# Revit family: 1000_Sliding_Window_XOX_Standard
name_source: partatom
category: Windows
revit_build: Autodesk Revit 2014 (Build: 20130308_1515(x64)
units: mm (PartAtom-declared; Revit-internal decimal feet)

## types (120) — shared parameters
Centered In Wall = Yes
Custom Sash Width Middle = 100 mm  [stored 0.328084 ft]
Default Sill Height = 800 mm
Description = Sliding window, XOX
Equal Sash Width = Yes
Frame Thickness = 76 mm
Limit Sash Height Max = 1800 mm  [stored 5.90551 ft]
Limit Sash Height Min = 300 mm
Limit Sash Width Max = 1500 mm  [stored 4.92126 ft]
Limit Sash Width Middle Min = 300 mm
Limit Sash Width Min = 300 mm
Limit Window Height Max = 1857 mm
Limit Window Height Min = 357 mm
Limit Window Width Max = 4440 mm
Limit Window Width Min = 840 mm
Manufacturer = Crealco
Model = 1000
Sash Frame Seal = 2 mm  [stored 0.00656168 ft]
URL = http://www.crealco.co.za
Wall Closure = By host
zero-valued in all types: Custom Frame Offset From Exterior

## per-type parameters (varying)
| type | Area Middle Sash Glazing | Area Side Sash Glazing | Clearvue SHGC Value | Clearvue U Value | Custom Windload | Custom Window Height | Custom Window Width | Energy Advantage SHGC Value | Energy Advantage U Value | Heavy Duty Interlocker | Height | Intruderprufe LowE SHGC Value | Intruderprufe LowE U Value | Intruderprufe SHGC Value | Intruderprufe U Value | Is Heavy Duty Mullion | Limit Sash Width Middle Max | Max Pane Area | Sash Height | Sash Width Middle | Sash Width Sides | Standard Interlocker | Width | Windload Design |
| 1000SW-0906XOX-1000Pa | 0.09 m² | 0.09 m² | 0.535 | 6.31 | 1000 mm  [stored 3.28084 ft] | 590 mm  [stored 1.9357 ft] | 890 mm  [stored 2.91995 ft] | 0.482 | 5.4 | No | 590 mm  [stored 1.9357 ft] | 0.444 | 5.12 | 0.508 | 5.99 | 0 mm  [stored 0 ft] | 350 mm | 0.09 m² | 533 mm | 317 mm | 317 mm | Yes | 890 mm  [stored 2.91995 ft] | 1000 mm  [stored 3.28084 ft] |
| 1000SW-1206XOX-1000Pa | 0.14 m² | 0.14 m² | 0.557 | 6.4 | 1000 mm  [stored 3.28084 ft] | 590 mm  [stored 1.9357 ft] | 1190 mm  [stored 3.9042 ft] | 0.5 | 5.34 | No | 590 mm  [stored 1.9357 ft] | 0.46 | 5.05 | 0.527 | 6.06 | 0 mm  [stored 0 ft] | 650 mm | 0.14 m² | 533 mm | 417 mm | 417 mm | Yes | 1190 mm  [stored 3.9042 ft] | 1000 mm  [stored 3.28084 ft] |
| 1000SW-1506XOX-1000Pa | 0.18 m² | 0.18 m² | 0.569 | 6.45 | 1000 mm  [stored 3.28084 ft] | 590 mm  [stored 1.9357 ft] | 1490 mm  [stored 4.88845 ft] | 0.511 | 5.31 | No | 590 mm  [stored 1.9357 ft] | 0.47 | 5.01 | 0.539 | 6.1 | 0 mm  [stored 0 ft] | 950 mm | 0.18 m² | 533 mm | 517 mm | 517 mm | Yes | 1490 mm  [stored 4.88845 ft] | 1000 mm  [stored 3.28084 ft] |
| 1000SW-1806XOX-1000Pa | 0.22 m² | 0.22 m² | 0.578 | 6.48 | 1000 mm  [stored 3.28084 ft] | 590 mm  [stored 1.9357 ft] | 1790 mm  [stored 5.8727 ft] | 0.519 | 5.29 | No | 590 mm  [stored 1.9357 ft] | 0.476 | 4.98 | 0.547 | 6.13 | 0 mm  [stored 0 ft] | 1250 mm | 0.22 m² | 533 mm | 617 mm | 617 mm | Yes | 1790 mm  [stored 5.8727 ft] | 1000 mm  [stored 3.28084 ft] |
| 1000SW-2106XOX-1000Pa | 0.27 m² | 0.27 m² | 0.584 | 6.51 | 1000 mm  [stored 3.28084 ft] | 590 mm  [stored 1.9357 ft] | 2090 mm  [stored 6.85696 ft] | 0.524 | 5.27 | No | 590 mm  [stored 1.9357 ft] | 0.481 | 4.96 | 0.552 | 6.15 | 0 mm  [stored 0 ft] | 1500 mm  [stored 4.92126 ft] | 0.27 m² | 533 mm | 717 mm | 717 mm | Yes | 2090 mm  [stored 6.85696 ft] | 1000 mm  [stored 3.28084 ft] |
| 1000SW-2406XOX-1000Pa | 0.31 m² | 0.31 m² | 0.588 | 6.52 | 1000 mm  [stored 3.28084 ft] | 590 mm  [stored 1.9357 ft] | 2390 mm  [stored 7.84121 ft] | 0.528 | 5.26 | No | 590 mm  [stored 1.9357 ft] | 0.484 | 4.95 | 0.556 | 6.16 | 0 mm  [stored 0 ft] | 1500 mm  [stored 4.92126 ft] | 0.31 m² | 533 mm | 817 mm | 817 mm | Yes | 2390 mm  [stored 7.84121 ft] | 1000 mm  [stored 3.28084 ft] |
| 1000SW-2706XOX-1000Pa | 0.35 m² | 0.35 m² | 0.592 | 6.54 | 1000 mm  [stored 3.28084 ft] | 590 mm  [stored 1.9357 ft] | 2690 mm | 0.531 | 5.25 | No | 590 mm  [stored 1.9357 ft] | 0.487 | 4.94 | 0.559 | 6.17 | 0 mm  [stored 0 ft] | 1500 mm  [stored 4.92126 ft] | 0.35 m² | 533 mm | 917 mm | 917 mm | Yes | 2690 mm | 1000 mm  [stored 3.28084 ft] |
| 1000SW-3006XOX-1000Pa | 0.4 m² | 0.4 m² | 0.595 | 6.55 | 1000 mm  [stored 3.28084 ft] | 590 mm  [stored 1.9357 ft] | 2990 mm  [stored 9.80971 ft] | 0.533 | 5.24 | No | 590 mm  [stored 1.9357 ft] | 0.489 | 4.93 | 0.562 | 6.18 | 0 mm  [stored 0 ft] | 1500 mm  [stored 4.92126 ft] | 0.4 m² | 533 mm | 1017 mm | 1017 mm | Yes | 2990 mm  [stored 9.80971 ft] | 1000 mm  [stored 3.28084 ft] |
| 1000SW-0909XOX-1000Pa | 0.16 m² | 0.16 m² | 0.603 | 6.11 | 1000 mm  [stored 3.28084 ft] | 890 mm  [stored 2.91995 ft] | 890 mm  [stored 2.91995 ft] | 0.541 | 5.06 | No | 890 mm  [stored 2.91995 ft] | 0.502 | 4.85 | 0.573 | 5.85 | 0 mm  [stored 0 ft] | 350 mm | 0.16 m² | 833 mm | 317 mm | 317 mm | Yes | 890 mm  [stored 2.91995 ft] | 1000 mm  [stored 3.28084 ft] |
| 1000SW-1209XOX-1000Pa | 0.23 m² | 0.23 m² | 0.626 | 6.18 | 1000 mm  [stored 3.28084 ft] | 890 mm  [stored 2.91995 ft] | 1190 mm  [stored 3.9042 ft] | 0.562 | 4.96 | No | 890 mm  [stored 2.91995 ft] | 0.52 | 4.74 | 0.595 | 5.91 | 0 mm  [stored 0 ft] | 650 mm | 0.23 m² | 833 mm | 417 mm | 417 mm | Yes | 1190 mm  [stored 3.9042 ft] | 1000 mm  [stored 3.28084 ft] |
| 1000SW-1509XOX-1000Pa | 0.3 m² | 0.3 m² | 0.641 | 6.22 | 1000 mm  [stored 3.28084 ft] | 890 mm  [stored 2.91995 ft] | 1490 mm  [stored 4.88845 ft] | 0.575 | 4.9 | No | 890 mm  [stored 2.91995 ft] | 0.531 | 4.68 | 0.608 | 5.95 | 0 mm  [stored 0 ft] | 950 mm | 0.3 m² | 833 mm | 517 mm | 517 mm | Yes | 1490 mm  [stored 4.88845 ft] | 1000 mm  [stored 3.28084 ft] |
| 1000SW-1809XOX-1000Pa | 0.38 m² | 0.38 m² | 0.65 | 6.25 | 1000 mm  [stored 3.28084 ft] | 890 mm  [stored 2.91995 ft] | 1790 mm  [stored 5.8727 ft] | 0.583 | 4.87 | No | 890 mm  [stored 2.91995 ft] | 0.538 | 4.64 | 0.616 | 5.97 | 0 mm  [stored 0 ft] | 1250 mm | 0.38 m² | 833 mm | 617 mm | 617 mm | Yes | 1790 mm  [stored 5.8727 ft] | 1000 mm  [stored 3.28084 ft] |
| 1000SW-2109XOX-1000Pa | 0.45 m² | 0.45 m² | 0.657 | 6.27 | 1000 mm  [stored 3.28084 ft] | 890 mm  [stored 2.91995 ft] | 2090 mm  [stored 6.85696 ft] | 0.589 | 4.84 | No | 890 mm  [stored 2.91995 ft] | 0.543 | 4.61 | 0.622 | 5.99 | 0 mm  [stored 0 ft] | 1500 mm  [stored 4.92126 ft] | 0.45 m² | 833 mm | 717 mm | 717 mm | Yes | 2090 mm  [stored 6.85696 ft] | 1000 mm  [stored 3.28084 ft] |
| 1000SW-2409XOX-1000Pa | 0.52 m² | 0.52 m² | 0.662 | 6.28 | 1000 mm  [stored 3.28084 ft] | 890 mm  [stored 2.91995 ft] | 2390 mm  [stored 7.84121 ft] | 0.593 | 4.82 | No | 890 mm  [stored 2.91995 ft] | 0.547 | 4.59 | 0.627 | 6 | 0 mm  [stored 0 ft] | 1500 mm  [stored 4.92126 ft] | 0.52 m² | 833 mm | 817 mm | 817 mm | Yes | 2390 mm  [stored 7.84121 ft] | 1000 mm  [stored 3.28084 ft] |
| 1000SW-2709XOX-1000Pa | 0.6 m² | 0.6 m² | 0.666 | 6.3 | 1000 mm  [stored 3.28084 ft] | 890 mm  [stored 2.91995 ft] | 2690 mm | 0.597 | 4.8 | No | 890 mm  [stored 2.91995 ft] | 0.55 | 4.57 | 0.631 | 6.01 | 0 mm  [stored 0 ft] | 1500 mm  [stored 4.92126 ft] | 0.6 m² | 833 mm | 917 mm | 917 mm | Yes | 2690 mm | 1000 mm  [stored 3.28084 ft] |
| 1000SW-3009XOX-1000Pa | 0.67 m² | 0.67 m² | 0.669 | 6.31 | 1000 mm  [stored 3.28084 ft] | 890 mm  [stored 2.91995 ft] | 2990 mm  [stored 9.80971 ft] | 0.599 | 4.79 | No | 890 mm  [stored 2.91995 ft] | 0.553 | 4.56 | 0.634 | 6.02 | 0 mm  [stored 0 ft] | 1500 mm  [stored 4.92126 ft] | 0.67 m² | 833 mm | 1017 mm | 1017 mm | Yes | 2990 mm  [stored 9.80971 ft] | 1000 mm  [stored 3.28084 ft] |
| 1000SW-0912XOX-1000Pa | 0.22 m² | 0.22 m² | 0.636 | 6.01 | 1000 mm  [stored 3.28084 ft] | 1190 mm  [stored 3.9042 ft] | 890 mm  [stored 2.91995 ft] | 0.571 | 4.89 | No | 1190 mm  [stored 3.9042 ft] | 0.531 | 4.71 | 0.605 | 5.78 | 0 mm  [stored 0 ft] | 350 mm | 0.22 m² | 1133 mm | 317 mm | 317 mm | Yes | 890 mm  [stored 2.91995 ft] | 1000 mm  [stored 3.28084 ft] |
| 1000SW-1212XOX-1000Pa | 0.33 m² | 0.33 m² | 0.661 | 6.07 | 1000 mm  [stored 3.28084 ft] | 1190 mm  [stored 3.9042 ft] | 1190 mm  [stored 3.9042 ft] | 0.593 | 4.77 | No | 1190 mm  [stored 3.9042 ft] | 0.55 | 4.59 | 0.628 | 5.84 | 0 mm  [stored 0 ft] | 650 mm | 0.33 m² | 1133 mm | 417 mm | 417 mm | Yes | 1190 mm  [stored 3.9042 ft] | 1000 mm  [stored 3.28084 ft] |
| 1000SW-1512XOX-1000Pa | 0.43 m² | 0.43 m² | 0.676 | 6.11 | 1000 mm  [stored 3.28084 ft] | 1190 mm  [stored 3.9042 ft] | 1490 mm  [stored 4.88845 ft] | 0.606 | 4.7 | No | 1190 mm  [stored 3.9042 ft] | 0.562 | 4.52 | 0.642 | 5.87 | 0 mm  [stored 0 ft] | 950 mm | 0.43 m² | 1133 mm | 517 mm | 517 mm | Yes | 1490 mm  [stored 4.88845 ft] | 1000 mm  [stored 3.28084 ft] |
| 1000SW-1812XOX-1000Pa | 0.53 m² | 0.53 m² | 0.686 | 6.13 | 1000 mm  [stored 3.28084 ft] | 1190 mm  [stored 3.9042 ft] | 1790 mm  [stored 5.8727 ft] | 0.615 | 4.66 | No | 1190 mm  [stored 3.9042 ft] | 0.569 | 4.47 | 0.651 | 5.89 | 0 mm  [stored 0 ft] | 1250 mm | 0.53 m² | 1133 mm | 617 mm | 617 mm | Yes | 1790 mm  [stored 5.8727 ft] | 1000 mm  [stored 3.28084 ft] |
| 1000SW-2112XOX-1000Pa | 0.64 m² | 0.64 m² | 0.693 | 6.15 | 1000 mm  [stored 3.28084 ft] | 1190 mm  [stored 3.9042 ft] | 2090 mm  [stored 6.85696 ft] | 0.621 | 4.63 | No | 1190 mm  [stored 3.9042 ft] | 0.575 | 4.44 | 0.657 | 5.91 | 0 mm  [stored 0 ft] | 1500 mm  [stored 4.92126 ft] | 0.64 m² | 1133 mm | 717 mm | 717 mm | Yes | 2090 mm  [stored 6.85696 ft] | 1000 mm  [stored 3.28084 ft] |
| 1000SW-2412XOX-1000Pa | 0.74 m² | 0.74 m² | 0.699 | 6.17 | 1000 mm  [stored 3.28084 ft] | 1190 mm  [stored 3.9042 ft] | 2390 mm  [stored 7.84121 ft] | 0.625 | 4.6 | No | 1190 mm  [stored 3.9042 ft] | 0.579 | 4.41 | 0.662 | 5.92 | 0 mm  [stored 0 ft] | 1500 mm  [stored 4.92126 ft] | 0.74 m² | 1133 mm | 817 mm | 817 mm | Yes | 2390 mm  [stored 7.84121 ft] | 1000 mm  [stored 3.28084 ft] |
| 1000SW-2712XOX-1000Pa | 0.84 m² | 0.84 m² | 0.703 | 6.18 | 1000 mm  [stored 3.28084 ft] | 1190 mm  [stored 3.9042 ft] | 2690 mm | 0.629 | 4.58 | No | 1190 mm  [stored 3.9042 ft] | 0.582 | 4.39 | 0.666 | 5.93 | 0 mm  [stored 0 ft] | 1500 mm  [stored 4.92126 ft] | 0.84 m² | 1133 mm | 917 mm | 917 mm | Yes | 2690 mm | 1000 mm  [stored 3.28084 ft] |
| 1000SW-3012XOX-1000Pa | 0.95 m² | 0.95 m² | 0.706 | 6.19 | 1000 mm  [stored 3.28084 ft] | 1190 mm  [stored 3.9042 ft] | 2990 mm  [stored 9.80971 ft] | 0.632 | 4.57 | No | 1190 mm  [stored 3.9042 ft] | 0.584 | 4.38 | 0.669 | 5.94 | 0 mm  [stored 0 ft] | 1500 mm  [stored 4.92126 ft] | 0.95 m² | 1133 mm | 1017 mm | 1017 mm | Yes | 2990 mm  [stored 9.80971 ft] | 1000 mm  [stored 3.28084 ft] |
| 1000SW-0915XOX-1000Pa | 0.29 m² | 0.29 m² | 0.656 | 5.95 | 1000 mm  [stored 3.28084 ft] | 1490 mm  [stored 4.88845 ft] | 890 mm  [stored 2.91995 ft] | 0.589 | 4.79 | No | 1490 mm  [stored 4.88845 ft] | 0.548 | 4.63 | 0.624 | 5.74 | 0 mm  [stored 0 ft] | 350 mm | 0.29 m² | 1433 mm | 317 mm | 317 mm | Yes | 890 mm  [stored 2.91995 ft] | 1000 mm  [stored 3.28084 ft] |
| 1000SW-1215XOX-1000Pa | 0.42 m² | 0.42 m² | 0.682 | 6.01 | 1000 mm  [stored 3.28084 ft] | 1490 mm  [stored 4.88845 ft] | 1190 mm  [stored 3.9042 ft] | 0.611 | 4.66 | No | 1490 mm  [stored 4.88845 ft] | 0.568 | 4.5 | 0.648 | 5.79 | 0 mm  [stored 0 ft] | 650 mm | 0.42 m² | 1433 mm | 417 mm | 417 mm | Yes | 1190 mm  [stored 3.9042 ft] | 1000 mm  [stored 3.28084 ft] |
| 1000SW-1515XOX-1000Pa | 0.55 m² | 0.55 m² | 0.698 | 6.04 | 1000 mm  [stored 3.28084 ft] | 1490 mm  [stored 4.88845 ft] | 1490 mm  [stored 4.88845 ft] | 0.625 | 4.58 | No | 1490 mm  [stored 4.88845 ft] | 0.58 | 4.42 | 0.662 | 5.83 | 0 mm  [stored 0 ft] | 950 mm | 0.55 m² | 1433 mm | 517 mm | 517 mm | Yes | 1490 mm  [stored 4.88845 ft] | 1000 mm  [stored 3.28084 ft] |
| 1000SW-1815XOX-1000Pa | 0.69 m² | 0.69 m² | 0.708 | 6.07 | 1000 mm  [stored 3.28084 ft] | 1490 mm  [stored 4.88845 ft] | 1790 mm  [stored 5.8727 ft] | 0.634 | 4.53 | No | 1490 mm  [stored 4.88845 ft] | 0.588 | 4.37 | 0.672 | 5.85 | 0 mm  [stored 0 ft] | 1250 mm | 0.69 m² | 1433 mm | 617 mm | 617 mm | Yes | 1790 mm  [stored 5.8727 ft] | 1000 mm  [stored 3.28084 ft] |
| 1000SW-2115XOX-1000Pa | 0.82 m² | 0.82 m² | 0.715 | 6.08 | 1000 mm  [stored 3.28084 ft] | 1490 mm  [stored 4.88845 ft] | 2090 mm  [stored 6.85696 ft] | 0.64 | 4.5 | No | 1490 mm  [stored 4.88845 ft] | 0.593 | 4.33 | 0.678 | 5.86 | 0 mm  [stored 0 ft] | 1500 mm  [stored 4.92126 ft] | 0.82 m² | 1433 mm | 717 mm | 717 mm | Yes | 2090 mm  [stored 6.85696 ft] | 1000 mm  [stored 3.28084 ft] |
| 1000SW-2415XOX-1000Pa | 0.95 m² | 0.95 m² | 0.721 | 6.1 | 1000 mm  [stored 3.28084 ft] | 1490 mm  [stored 4.88845 ft] | 2390 mm  [stored 7.84121 ft] | 0.645 | 4.47 | No | 1490 mm  [stored 4.88845 ft] | 0.597 | 4.31 | 0.683 | 5.87 | 0 mm  [stored 0 ft] | 1500 mm  [stored 4.92126 ft] | 0.95 m² | 1433 mm | 817 mm | 817 mm | Yes | 2390 mm  [stored 7.84121 ft] | 1000 mm  [stored 3.28084 ft] |
| 1000SW-2715XOX-1000Pa | 1.09 m² | 1.09 m² | 0.725 | 6.11 | 1000 mm  [stored 3.28084 ft] | 1490 mm  [stored 4.88845 ft] | 2690 mm | 0.648 | 4.45 | No | 1490 mm  [stored 4.88845 ft] | 0.601 | 4.29 | 0.687 | 5.88 | 0 mm  [stored 0 ft] | 1500 mm  [stored 4.92126 ft] | 1.09 m² | 1433 mm | 917 mm | 917 mm | Yes | 2690 mm | 1000 mm  [stored 3.28084 ft] |
| 1000SW-3015XOX-1000Pa | 1.22 m² | 1.22 m² | 0.728 | 6.11 | 1000 mm  [stored 3.28084 ft] | 1490 mm  [stored 4.88845 ft] | 2990 mm  [stored 9.80971 ft] | 0.651 | 4.44 | No | 1490 mm  [stored 4.88845 ft] | 0.603 | 4.207 | 0.69 | 5.89 | 0 mm  [stored 0 ft] | 1500 mm  [stored 4.92126 ft] | 1.22 m² | 1433 mm | 1017 mm | 1017 mm | Yes | 2990 mm  [stored 9.80971 ft] | 1000 mm  [stored 3.28084 ft] |
| 1000SW-0918XOX-1000Pa | 0.35 m² | 0.35 m² | 0.669 | 5.91 | 1000 mm  [stored 3.28084 ft] | 1790 mm  [stored 5.8727 ft] | 890 mm  [stored 2.91995 ft] | 0.6 | 4.72 | No | 1790 mm  [stored 5.8727 ft] | 0.559 | 4.58 | 0.637 | 5.71 | 0 mm  [stored 0 ft] | 350 mm | 0.35 m² | 1733 mm | 317 mm | 317 mm | Yes | 890 mm  [stored 2.91995 ft] | 1000 mm  [stored 3.28084 ft] |
| 1000SW-1218XOX-1000Pa | 0.52 m² | 0.52 m² | 0.696 | 5.96 | 1000 mm  [stored 3.28084 ft] | 1790 mm  [stored 5.8727 ft] | 1190 mm  [stored 3.9042 ft] | 0.623 | 4.59 | No | 1790 mm  [stored 5.8727 ft] | 0.58 | 4.44 | 0.661 | 5.76 | 0 mm  [stored 0 ft] | 650 mm | 0.52 m² | 1733 mm | 417 mm | 417 mm | Yes | 1190 mm  [stored 3.9042 ft] | 1000 mm  [stored 3.28084 ft] |
| 1000SW-1518XOX-1000Pa | 0.68 m² | 0.68 m² | 0.712 | 6 | 1000 mm  [stored 3.28084 ft] | 1790 mm  [stored 5.8727 ft] | 1490 mm  [stored 4.88845 ft] | 0.637 | 4.51 | No | 1790 mm  [stored 5.8727 ft] | 0.592 | 4.36 | 0.676 | 5.8 | 0 mm  [stored 0 ft] | 950 mm | 0.68 m² | 1733 mm | 517 mm | 517 mm | Yes | 1490 mm  [stored 4.88845 ft] | 1000 mm  [stored 3.28084 ft] |
| 1000SW-1818XOX-1000Pa | 0.84 m² | 0.84 m² | 0.722 | 6.02 | 1000 mm  [stored 3.28084 ft] | 1790 mm  [stored 5.8727 ft] | 1790 mm  [stored 5.8727 ft] | 0.646 | 4.45 | Yes | 1790 mm  [stored 5.8727 ft] | 0.6 | 4.3 | 0.685 | 5.82 | 1 mm  [stored 0.00328084 ft] | 1250 mm | 0.84 m² | 1733 mm | 617 mm | 617 mm | No | 1790 mm  [stored 5.8727 ft] | 1000 mm  [stored 3.28084 ft] |
| 1000SW-2118XOX-1000Pa | 1.01 m² | 1.01 m² | 0.73 | 6.04 | 1000 mm  [stored 3.28084 ft] | 1790 mm  [stored 5.8727 ft] | 2090 mm  [stored 6.85696 ft] | 0.653 | 4.41 | Yes | 1790 mm  [stored 5.8727 ft] | 0.606 | 4.27 | 0.692 | 5.83 | 1 mm  [stored 0.00328084 ft] | 1500 mm  [stored 4.92126 ft] | 1.01 m² | 1733 mm | 717 mm | 717 mm | No | 2090 mm  [stored 6.85696 ft] | 1000 mm  [stored 3.28084 ft] |
| 1000SW-2418XOX-1000Pa | 1.17 m² | 1.17 m² | 0.735 | 6.05 | 1000 mm  [stored 3.28084 ft] | 1790 mm  [stored 5.8727 ft] | 2390 mm  [stored 7.84121 ft] | 0.658 | 4.39 | Yes | 1790 mm  [stored 5.8727 ft] | 0.61 | 4.24 | 0.697 | 5.84 | 1 mm  [stored 0.00328084 ft] | 1500 mm  [stored 4.92126 ft] | 1.17 m² | 1733 mm | 817 mm | 817 mm | No | 2390 mm  [stored 7.84121 ft] | 1000 mm  [stored 3.28084 ft] |
| 1000SW-2718XOX-1000Pa | 1.33 m² | 1.33 m² | 0.74 | 6.06 | 1000 mm  [stored 3.28084 ft] | 1790 mm  [stored 5.8727 ft] | 2690 mm | 0.661 | 4.36 | Yes | 1790 mm  [stored 5.8727 ft] | 0.613 | 4.21 | 0.701 | 5.85 | 1 mm  [stored 0.00328084 ft] | 1500 mm  [stored 4.92126 ft] | 1.33 m² | 1733 mm | 917 mm | 917 mm | No | 2690 mm | 1000 mm  [stored 3.28084 ft] |
| 1000SW-3018XOX-1000Pa | 1.49 m² | 1.5 m² | 0.743 | 6.07 | 1000 mm  [stored 3.28084 ft] | 1790 mm  [stored 5.8727 ft] | 2990 mm  [stored 9.80971 ft] | 0.664 | 4.35 | Yes | 1790 mm  [stored 5.8727 ft] | 0.616 | 4.2 | 0.704 | 5.86 | 1 mm  [stored 0.00328084 ft] | 1500 mm  [stored 4.92126 ft] | 1.5 m² | 1733 mm | 1017 mm | 1017 mm | No | 2990 mm  [stored 9.80971 ft] | 1000 mm  [stored 3.28084 ft] |
| 1000SW-0906XOX-1500Pa | 0.09 m² | 0.09 m² | 0.535 | 6.31 | 1500 mm  [stored 4.92126 ft] | 590 mm  [stored 1.9357 ft] | 890 mm  [stored 2.91995 ft] | 0.482 | 5.4 | No | 590 mm  [stored 1.9357 ft] | 0.444 | 5.12 | 0.508 | 5.99 | 0 mm  [stored 0 ft] | 350 mm | 0.09 m² | 533 mm | 317 mm | 317 mm | Yes | 890 mm  [stored 2.91995 ft] | 1500 mm  [stored 4.92126 ft] |
| 1000SW-0906XOX-2000Pa | 0.09 m² | 0.09 m² | 0.535 | 6.31 | 2000 mm  [stored 6.56168 ft] | 590 mm  [stored 1.9357 ft] | 890 mm  [stored 2.91995 ft] | 0.482 | 5.4 | No | 590 mm  [stored 1.9357 ft] | 0.444 | 5.12 | 0.508 | 5.99 | 0 mm  [stored 0 ft] | 350 mm | 0.09 m² | 533 mm | 317 mm | 317 mm | Yes | 890 mm  [stored 2.91995 ft] | 2000 mm  [stored 6.56168 ft] |
| 1000SW-0909XOX-1500Pa | 0.16 m² | 0.16 m² | 0.603 | 6.11 | 1500 mm  [stored 4.92126 ft] | 890 mm  [stored 2.91995 ft] | 890 mm  [stored 2.91995 ft] | 0.541 | 5.06 | No | 890 mm  [stored 2.91995 ft] | 0.502 | 4.85 | 0.573 | 5.85 | 0 mm  [stored 0 ft] | 350 mm | 0.16 m² | 833 mm | 317 mm | 317 mm | Yes | 890 mm  [stored 2.91995 ft] | 1500 mm  [stored 4.92126 ft] |
| 1000SW-0909XOX-2000Pa | 0.16 m² | 0.16 m² | 0.603 | 6.11 | 2000 mm  [stored 6.56168 ft] | 890 mm  [stored 2.91995 ft] | 890 mm  [stored 2.91995 ft] | 0.541 | 5.06 | No | 890 mm  [stored 2.91995 ft] | 0.502 | 4.85 | 0.573 | 5.85 | 0 mm  [stored 0 ft] | 350 mm | 0.16 m² | 833 mm | 317 mm | 317 mm | Yes | 890 mm  [stored 2.91995 ft] | 2000 mm  [stored 6.56168 ft] |
| 1000SW-0912XOX-1500Pa | 0.22 m² | 0.22 m² | 0.636 | 6.01 | 1500 mm  [stored 4.92126 ft] | 1190 mm  [stored 3.9042 ft] | 890 mm  [stored 2.91995 ft] | 0.571 | 4.89 | No | 1190 mm  [stored 3.9042 ft] | 0.531 | 4.71 | 0.605 | 5.78 | 0 mm  [stored 0 ft] | 350 mm | 0.22 m² | 1133 mm | 317 mm | 317 mm | Yes | 890 mm  [stored 2.91995 ft] | 1500 mm  [stored 4.92126 ft] |
| 1000SW-0912XOX-2000Pa | 0.22 m² | 0.22 m² | 0.636 | 6.01 | 2000 mm  [stored 6.56168 ft] | 1190 mm  [stored 3.9042 ft] | 890 mm  [stored 2.91995 ft] | 0.571 | 4.89 | No | 1190 mm  [stored 3.9042 ft] | 0.531 | 4.71 | 0.605 | 5.78 | 0 mm  [stored 0 ft] | 350 mm | 0.22 m² | 1133 mm | 317 mm | 317 mm | Yes | 890 mm  [stored 2.91995 ft] | 2000 mm  [stored 6.56168 ft] |
| 1000SW-0915XOX-1500Pa | 0.29 m² | 0.29 m² | 0.656 | 5.95 | 1500 mm  [stored 4.92126 ft] | 1490 mm  [stored 4.88845 ft] | 890 mm  [stored 2.91995 ft] | 0.589 | 4.79 | No | 1490 mm  [stored 4.88845 ft] | 0.548 | 4.63 | 0.624 | 5.74 | 0 mm  [stored 0 ft] | 350 mm | 0.29 m² | 1433 mm | 317 mm | 317 mm | Yes | 890 mm  [stored 2.91995 ft] | 1500 mm  [stored 4.92126 ft] |
| 1000SW-0915XOX-2000Pa | 0.29 m² | 0.29 m² | 0.656 | 5.95 | 2000 mm  [stored 6.56168 ft] | 1490 mm  [stored 4.88845 ft] | 890 mm  [stored 2.91995 ft] | 0.589 | 4.79 | No | 1490 mm  [stored 4.88845 ft] | 0.548 | 4.63 | 0.624 | 5.74 | 0 mm  [stored 0 ft] | 350 mm | 0.29 m² | 1433 mm | 317 mm | 317 mm | Yes | 890 mm  [stored 2.91995 ft] | 2000 mm  [stored 6.56168 ft] |
| 1000SW-0918XOX-1500Pa | 0.35 m² | 0.35 m² | 0.669 | 5.91 | 1500 mm  [stored 4.92126 ft] | 1790 mm  [stored 5.8727 ft] | 890 mm  [stored 2.91995 ft] | 0.6 | 4.72 | No | 1790 mm  [stored 5.8727 ft] | 0.559 | 4.58 | 0.637 | 5.71 | 0 mm  [stored 0 ft] | 350 mm | 0.35 m² | 1733 mm | 317 mm | 317 mm | Yes | 890 mm  [stored 2.91995 ft] | 1500 mm  [stored 4.92126 ft] |
| 1000SW-0918XOX-2000Pa | 0.35 m² | 0.35 m² | 0.669 | 5.91 | 2000 mm  [stored 6.56168 ft] | 1790 mm  [stored 5.8727 ft] | 890 mm  [stored 2.91995 ft] | 0.6 | 4.72 | Yes | 1790 mm  [stored 5.8727 ft] | 0.559 | 4.58 | 0.637 | 5.71 | 1 mm  [stored 0.00328084 ft] | 350 mm | 0.35 m² | 1733 mm | 317 mm | 317 mm | No | 890 mm  [stored 2.91995 ft] | 2000 mm  [stored 6.56168 ft] |
| 1000SW-1206XOX-1500Pa | 0.14 m² | 0.14 m² | 0.557 | 6.4 | 1500 mm  [stored 4.92126 ft] | 590 mm  [stored 1.9357 ft] | 1190 mm  [stored 3.9042 ft] | 0.5 | 5.34 | No | 590 mm  [stored 1.9357 ft] | 0.46 | 5.05 | 0.527 | 6.06 | 0 mm  [stored 0 ft] | 650 mm | 0.14 m² | 533 mm | 417 mm | 417 mm | Yes | 1190 mm  [stored 3.9042 ft] | 1500 mm  [stored 4.92126 ft] |
| 1000SW-1206XOX-2000Pa | 0.14 m² | 0.14 m² | 0.557 | 6.4 | 2000 mm  [stored 6.56168 ft] | 590 mm  [stored 1.9357 ft] | 1190 mm  [stored 3.9042 ft] | 0.5 | 5.34 | No | 590 mm  [stored 1.9357 ft] | 0.46 | 5.05 | 0.527 | 6.06 | 0 mm  [stored 0 ft] | 650 mm | 0.14 m² | 533 mm | 417 mm | 417 mm | Yes | 1190 mm  [stored 3.9042 ft] | 2000 mm  [stored 6.56168 ft] |
| 1000SW-1209XOX-1500Pa | 0.23 m² | 0.23 m² | 0.626 | 6.18 | 1500 mm  [stored 4.92126 ft] | 890 mm  [stored 2.91995 ft] | 1190 mm  [stored 3.9042 ft] | 0.562 | 4.96 | No | 890 mm  [stored 2.91995 ft] | 0.52 | 4.74 | 0.595 | 5.91 | 0 mm  [stored 0 ft] | 650 mm | 0.23 m² | 833 mm | 417 mm | 417 mm | Yes | 1190 mm  [stored 3.9042 ft] | 1500 mm  [stored 4.92126 ft] |
| 1000SW-1209XOX-2000Pa | 0.23 m² | 0.23 m² | 0.626 | 6.18 | 2000 mm  [stored 6.56168 ft] | 890 mm  [stored 2.91995 ft] | 1190 mm  [stored 3.9042 ft] | 0.562 | 4.96 | No | 890 mm  [stored 2.91995 ft] | 0.52 | 4.74 | 0.595 | 5.91 | 0 mm  [stored 0 ft] | 650 mm | 0.23 m² | 833 mm | 417 mm | 417 mm | Yes | 1190 mm  [stored 3.9042 ft] | 2000 mm  [stored 6.56168 ft] |
| 1000SW-1212XOX-1500Pa | 0.33 m² | 0.33 m² | 0.661 | 6.07 | 1500 mm  [stored 4.92126 ft] | 1190 mm  [stored 3.9042 ft] | 1190 mm  [stored 3.9042 ft] | 0.593 | 4.77 | No | 1190 mm  [stored 3.9042 ft] | 0.55 | 4.59 | 0.628 | 5.84 | 0 mm  [stored 0 ft] | 650 mm | 0.33 m² | 1133 mm | 417 mm | 417 mm | Yes | 1190 mm  [stored 3.9042 ft] | 1500 mm  [stored 4.92126 ft] |
| 1000SW-1212XOX-2000Pa | 0.33 m² | 0.33 m² | 0.661 | 6.07 | 2000 mm  [stored 6.56168 ft] | 1190 mm  [stored 3.9042 ft] | 1190 mm  [stored 3.9042 ft] | 0.593 | 4.77 | No | 1190 mm  [stored 3.9042 ft] | 0.55 | 4.59 | 0.628 | 5.84 | 0 mm  [stored 0 ft] | 650 mm | 0.33 m² | 1133 mm | 417 mm | 417 mm | Yes | 1190 mm  [stored 3.9042 ft] | 2000 mm  [stored 6.56168 ft] |
| 1000SW-1215XOX-1500Pa | 0.42 m² | 0.42 m² | 0.682 | 6.01 | 1500 mm  [stored 4.92126 ft] | 1490 mm  [stored 4.88845 ft] | 1190 mm  [stored 3.9042 ft] | 0.611 | 4.66 | No | 1490 mm  [stored 4.88845 ft] | 0.568 | 4.5 | 0.648 | 5.79 | 0 mm  [stored 0 ft] | 650 mm | 0.42 m² | 1433 mm | 417 mm | 417 mm | Yes | 1190 mm  [stored 3.9042 ft] | 1500 mm  [stored 4.92126 ft] |
| 1000SW-1215XOX-2000Pa | 0.42 m² | 0.42 m² | 0.682 | 6.01 | 2000 mm  [stored 6.56168 ft] | 1490 mm  [stored 4.88845 ft] | 1190 mm  [stored 3.9042 ft] | 0.611 | 4.66 | No | 1490 mm  [stored 4.88845 ft] | 0.568 | 4.5 | 0.648 | 5.79 | 0 mm  [stored 0 ft] | 650 mm | 0.42 m² | 1433 mm | 417 mm | 417 mm | Yes | 1190 mm  [stored 3.9042 ft] | 2000 mm  [stored 6.56168 ft] |
| 1000SW-1218XOX-1500Pa | 0.52 m² | 0.52 m² | 0.696 | 5.96 | 1500 mm  [stored 4.92126 ft] | 1790 mm  [stored 5.8727 ft] | 1190 mm  [stored 3.9042 ft] | 0.623 | 4.59 | Yes | 1790 mm  [stored 5.8727 ft] | 0.58 | 4.44 | 0.661 | 5.76 | 1 mm  [stored 0.00328084 ft] | 650 mm | 0.52 m² | 1733 mm | 417 mm | 417 mm | No | 1190 mm  [stored 3.9042 ft] | 1500 mm  [stored 4.92126 ft] |
| 1000SW-1218XOX-2000Pa | 0.52 m² | 0.52 m² | 0.696 | 5.96 | 2000 mm  [stored 6.56168 ft] | 1790 mm  [stored 5.8727 ft] | 1190 mm  [stored 3.9042 ft] | 0.623 | 4.59 | Yes | 1790 mm  [stored 5.8727 ft] | 0.58 | 4.44 | 0.661 | 5.76 | 1 mm  [stored 0.00328084 ft] | 650 mm | 0.52 m² | 1733 mm | 417 mm | 417 mm | No | 1190 mm  [stored 3.9042 ft] | 2000 mm  [stored 6.56168 ft] |
| 1000SW-1506XOX-1500Pa | 0.18 m² | 0.18 m² | 0.569 | 6.45 | 1500 mm  [stored 4.92126 ft] | 590 mm  [stored 1.9357 ft] | 1490 mm  [stored 4.88845 ft] | 0.511 | 5.31 | No | 590 mm  [stored 1.9357 ft] | 0.47 | 5.01 | 0.539 | 6.1 | 0 mm  [stored 0 ft] | 950 mm | 0.18 m² | 533 mm | 517 mm | 517 mm | Yes | 1490 mm  [stored 4.88845 ft] | 1500 mm  [stored 4.92126 ft] |
| 1000SW-1506XOX-2000Pa | 0.18 m² | 0.18 m² | 0.569 | 6.45 | 2000 mm  [stored 6.56168 ft] | 590 mm  [stored 1.9357 ft] | 1490 mm  [stored 4.88845 ft] | 0.511 | 5.31 | No | 590 mm  [stored 1.9357 ft] | 0.47 | 5.01 | 0.539 | 6.1 | 0 mm  [stored 0 ft] | 950 mm | 0.18 m² | 533 mm | 517 mm | 517 mm | Yes | 1490 mm  [stored 4.88845 ft] | 2000 mm  [stored 6.56168 ft] |
| 1000SW-1509XOX-1500Pa | 0.3 m² | 0.3 m² | 0.641 | 6.22 | 1500 mm  [stored 4.92126 ft] | 890 mm  [stored 2.91995 ft] | 1490 mm  [stored 4.88845 ft] | 0.575 | 4.9 | No | 890 mm  [stored 2.91995 ft] | 0.531 | 4.68 | 0.608 | 5.95 | 0 mm  [stored 0 ft] | 950 mm | 0.3 m² | 833 mm | 517 mm | 517 mm | Yes | 1490 mm  [stored 4.88845 ft] | 1500 mm  [stored 4.92126 ft] |
| 1000SW-1509XOX-2000Pa | 0.3 m² | 0.3 m² | 0.641 | 6.22 | 2000 mm  [stored 6.56168 ft] | 890 mm  [stored 2.91995 ft] | 1490 mm  [stored 4.88845 ft] | 0.575 | 4.9 | No | 890 mm  [stored 2.91995 ft] | 0.531 | 4.68 | 0.608 | 5.95 | 0 mm  [stored 0 ft] | 950 mm | 0.3 m² | 833 mm | 517 mm | 517 mm | Yes | 1490 mm  [stored 4.88845 ft] | 2000 mm  [stored 6.56168 ft] |
| 1000SW-1512XOX-1500Pa | 0.43 m² | 0.43 m² | 0.676 | 6.11 | 1500 mm  [stored 4.92126 ft] | 1190 mm  [stored 3.9042 ft] | 1490 mm  [stored 4.88845 ft] | 0.606 | 4.7 | No | 1190 mm  [stored 3.9042 ft] | 0.562 | 4.52 | 0.642 | 5.87 | 0 mm  [stored 0 ft] | 950 mm | 0.43 m² | 1133 mm | 517 mm | 517 mm | Yes | 1490 mm  [stored 4.88845 ft] | 1500 mm  [stored 4.92126 ft] |
| 1000SW-1512XOX-2000Pa | 0.43 m² | 0.43 m² | 0.676 | 6.11 | 2000 mm  [stored 6.56168 ft] | 1190 mm  [stored 3.9042 ft] | 1490 mm  [stored 4.88845 ft] | 0.606 | 4.7 | No | 1190 mm  [stored 3.9042 ft] | 0.562 | 4.52 | 0.642 | 5.87 | 0 mm  [stored 0 ft] | 950 mm | 0.43 m² | 1133 mm | 517 mm | 517 mm | Yes | 1490 mm  [stored 4.88845 ft] | 2000 mm  [stored 6.56168 ft] |
| 1000SW-1515XOX-1500Pa | 0.55 m² | 0.55 m² | 0.698 | 6.04 | 1500 mm  [stored 4.92126 ft] | 1490 mm  [stored 4.88845 ft] | 1490 mm  [stored 4.88845 ft] | 0.625 | 4.58 | No | 1490 mm  [stored 4.88845 ft] | 0.58 | 4.42 | 0.662 | 5.83 | 0 mm  [stored 0 ft] | 950 mm | 0.55 m² | 1433 mm | 517 mm | 517 mm | Yes | 1490 mm  [stored 4.88845 ft] | 1500 mm  [stored 4.92126 ft] |
| 1000SW-1515XOX-2000Pa | 0.55 m² | 0.55 m² | 0.698 | 6.04 | 2000 mm  [stored 6.56168 ft] | 1490 mm  [stored 4.88845 ft] | 1490 mm  [stored 4.88845 ft] | 0.625 | 4.58 | Yes | 1490 mm  [stored 4.88845 ft] | 0.58 | 4.42 | 0.662 | 5.83 | 1 mm  [stored 0.00328084 ft] | 950 mm | 0.55 m² | 1433 mm | 517 mm | 517 mm | No | 1490 mm  [stored 4.88845 ft] | 2000 mm  [stored 6.56168 ft] |
| 1000SW-1518XOX-1500Pa | 0.68 m² | 0.68 m² | 0.712 | 6 | 1500 mm  [stored 4.92126 ft] | 1790 mm  [stored 5.8727 ft] | 1490 mm  [stored 4.88845 ft] | 0.637 | 4.51 | Yes | 1790 mm  [stored 5.8727 ft] | 0.592 | 4.36 | 0.676 | 5.8 | 1 mm  [stored 0.00328084 ft] | 950 mm | 0.68 m² | 1733 mm | 517 mm | 517 mm | No | 1490 mm  [stored 4.88845 ft] | 1500 mm  [stored 4.92126 ft] |
| 1000SW-1518XOX-2000Pa | 0.68 m² | 0.68 m² | 0.712 | 6 | 2000 mm  [stored 6.56168 ft] | 1790 mm  [stored 5.8727 ft] | 1490 mm  [stored 4.88845 ft] | 0.637 | 4.51 | Yes | 1790 mm  [stored 5.8727 ft] | 0.592 | 4.36 | 0.676 | 5.8 | 1 mm  [stored 0.00328084 ft] | 950 mm | 0.68 m² | 1733 mm | 517 mm | 517 mm | No | 1490 mm  [stored 4.88845 ft] | 2000 mm  [stored 6.56168 ft] |
| 1000SW-1806XOX-1500Pa | 0.22 m² | 0.22 m² | 0.578 | 6.48 | 1500 mm  [stored 4.92126 ft] | 590 mm  [stored 1.9357 ft] | 1790 mm  [stored 5.8727 ft] | 0.519 | 5.29 | No | 590 mm  [stored 1.9357 ft] | 0.476 | 4.98 | 0.547 | 6.13 | 0 mm  [stored 0 ft] | 1250 mm | 0.22 m² | 533 mm | 617 mm | 617 mm | Yes | 1790 mm  [stored 5.8727 ft] | 1500 mm  [stored 4.92126 ft] |
| 1000SW-1806XOX-2000Pa | 0.22 m² | 0.22 m² | 0.578 | 6.48 | 2000 mm  [stored 6.56168 ft] | 590 mm  [stored 1.9357 ft] | 1790 mm  [stored 5.8727 ft] | 0.519 | 5.29 | No | 590 mm  [stored 1.9357 ft] | 0.476 | 4.98 | 0.547 | 6.13 | 0 mm  [stored 0 ft] | 1250 mm | 0.22 m² | 533 mm | 617 mm | 617 mm | Yes | 1790 mm  [stored 5.8727 ft] | 2000 mm  [stored 6.56168 ft] |
| 1000SW-1809XOX-1500Pa | 0.38 m² | 0.38 m² | 0.65 | 6.25 | 1500 mm  [stored 4.92126 ft] | 890 mm  [stored 2.91995 ft] | 1790 mm  [stored 5.8727 ft] | 0.583 | 4.87 | No | 890 mm  [stored 2.91995 ft] | 0.538 | 4.64 | 0.616 | 5.97 | 0 mm  [stored 0 ft] | 1250 mm | 0.38 m² | 833 mm | 617 mm | 617 mm | Yes | 1790 mm  [stored 5.8727 ft] | 1500 mm  [stored 4.92126 ft] |
| 1000SW-1809XOX-2000Pa | 0.38 m² | 0.38 m² | 0.65 | 6.25 | 2000 mm  [stored 6.56168 ft] | 890 mm  [stored 2.91995 ft] | 1790 mm  [stored 5.8727 ft] | 0.583 | 4.87 | No | 890 mm  [stored 2.91995 ft] | 0.538 | 4.64 | 0.616 | 5.97 | 0 mm  [stored 0 ft] | 1250 mm | 0.38 m² | 833 mm | 617 mm | 617 mm | Yes | 1790 mm  [stored 5.8727 ft] | 2000 mm  [stored 6.56168 ft] |
| 1000SW-1812XOX-1500Pa | 0.53 m² | 0.53 m² | 0.686 | 6.13 | 1500 mm  [stored 4.92126 ft] | 1190 mm  [stored 3.9042 ft] | 1790 mm  [stored 5.8727 ft] | 0.615 | 4.66 | No | 1190 mm  [stored 3.9042 ft] | 0.569 | 4.47 | 0.651 | 5.89 | 0 mm  [stored 0 ft] | 1250 mm | 0.53 m² | 1133 mm | 617 mm | 617 mm | Yes | 1790 mm  [stored 5.8727 ft] | 1500 mm  [stored 4.92126 ft] |
| 1000SW-1812XOX-2000Pa | 0.53 m² | 0.53 m² | 0.686 | 6.13 | 2000 mm  [stored 6.56168 ft] | 1190 mm  [stored 3.9042 ft] | 1790 mm  [stored 5.8727 ft] | 0.615 | 4.66 | No | 1190 mm  [stored 3.9042 ft] | 0.569 | 4.47 | 0.651 | 5.89 | 0 mm  [stored 0 ft] | 1250 mm | 0.53 m² | 1133 mm | 617 mm | 617 mm | Yes | 1790 mm  [stored 5.8727 ft] | 2000 mm  [stored 6.56168 ft] |
| 1000SW-1815XOX-1500Pa | 0.69 m² | 0.69 m² | 0.708 | 6.07 | 1500 mm  [stored 4.92126 ft] | 1490 mm  [stored 4.88845 ft] | 1790 mm  [stored 5.8727 ft] | 0.634 | 4.53 | No | 1490 mm  [stored 4.88845 ft] | 0.588 | 4.37 | 0.672 | 5.85 | 0 mm  [stored 0 ft] | 1250 mm | 0.69 m² | 1433 mm | 617 mm | 617 mm | Yes | 1790 mm  [stored 5.8727 ft] | 1500 mm  [stored 4.92126 ft] |
| 1000SW-1815XOX-2000Pa | 0.69 m² | 0.69 m² | 0.708 | 6.07 | 2000 mm  [stored 6.56168 ft] | 1490 mm  [stored 4.88845 ft] | 1790 mm  [stored 5.8727 ft] | 0.634 | 4.53 | Yes | 1490 mm  [stored 4.88845 ft] | 0.588 | 4.37 | 0.672 | 5.85 | 1 mm  [stored 0.00328084 ft] | 1250 mm | 0.69 m² | 1433 mm | 617 mm | 617 mm | No | 1790 mm  [stored 5.8727 ft] | 2000 mm  [stored 6.56168 ft] |
| 1000SW-1818XOX-1500Pa | 0.84 m² | 0.84 m² | 0.722 | 6.02 | 1500 mm  [stored 4.92126 ft] | 1790 mm  [stored 5.8727 ft] | 1790 mm  [stored 5.8727 ft] | 0.646 | 4.45 | Yes | 1790 mm  [stored 5.8727 ft] | 0.6 | 4.3 | 0.685 | 5.82 | 1 mm  [stored 0.00328084 ft] | 1250 mm | 0.84 m² | 1733 mm | 617 mm | 617 mm | No | 1790 mm  [stored 5.8727 ft] | 1500 mm  [stored 4.92126 ft] |
| 1000SW-1818XOX-2000Pa | 0.84 m² | 0.84 m² | 0.722 | 6.02 | 2000 mm  [stored 6.56168 ft] | 1790 mm  [stored 5.8727 ft] | 1790 mm  [stored 5.8727 ft] | 0.646 | 4.45 | Yes | 1790 mm  [stored 5.8727 ft] | 0.6 | 4.3 | 0.685 | 5.82 | 1 mm  [stored 0.00328084 ft] | 1250 mm | 0.84 m² | 1733 mm | 617 mm | 617 mm | No | 1790 mm  [stored 5.8727 ft] | 2000 mm  [stored 6.56168 ft] |
| 1000SW-2106XOX-1500Pa | 0.27 m² | 0.27 m² | 0.584 | 6.51 | 1500 mm  [stored 4.92126 ft] | 590 mm  [stored 1.9357 ft] | 2090 mm  [stored 6.85696 ft] | 0.524 | 5.27 | No | 590 mm  [stored 1.9357 ft] | 0.481 | 4.96 | 0.552 | 6.15 | 0 mm  [stored 0 ft] | 1500 mm  [stored 4.92126 ft] | 0.27 m² | 533 mm | 717 mm | 717 mm | Yes | 2090 mm  [stored 6.85696 ft] | 1500 mm  [stored 4.92126 ft] |
| 1000SW-2106XOX-2000Pa | 0.27 m² | 0.27 m² | 0.584 | 6.51 | 2000 mm  [stored 6.56168 ft] | 590 mm  [stored 1.9357 ft] | 2090 mm  [stored 6.85696 ft] | 0.524 | 5.27 | No | 590 mm  [stored 1.9357 ft] | 0.481 | 4.96 | 0.552 | 6.15 | 0 mm  [stored 0 ft] | 1500 mm  [stored 4.92126 ft] | 0.27 m² | 533 mm | 717 mm | 717 mm | Yes | 2090 mm  [stored 6.85696 ft] | 2000 mm  [stored 6.56168 ft] |
| 1000SW-2109XOX-1500Pa | 0.45 m² | 0.45 m² | 0.657 | 6.27 | 1500 mm  [stored 4.92126 ft] | 890 mm  [stored 2.91995 ft] | 2090 mm  [stored 6.85696 ft] | 0.589 | 4.84 | No | 890 mm  [stored 2.91995 ft] | 0.543 | 4.61 | 0.622 | 5.99 | 0 mm  [stored 0 ft] | 1500 mm  [stored 4.92126 ft] | 0.45 m² | 833 mm | 717 mm | 717 mm | Yes | 2090 mm  [stored 6.85696 ft] | 1500 mm  [stored 4.92126 ft] |
| 1000SW-2109XOX-2000Pa | 0.45 m² | 0.45 m² | 0.657 | 6.27 | 2000 mm  [stored 6.56168 ft] | 890 mm  [stored 2.91995 ft] | 2090 mm  [stored 6.85696 ft] | 0.589 | 4.84 | No | 890 mm  [stored 2.91995 ft] | 0.543 | 4.61 | 0.622 | 5.99 | 0 mm  [stored 0 ft] | 1500 mm  [stored 4.92126 ft] | 0.45 m² | 833 mm | 717 mm | 717 mm | Yes | 2090 mm  [stored 6.85696 ft] | 2000 mm  [stored 6.56168 ft] |
| 1000SW-2112XOX-1500Pa | 0.64 m² | 0.64 m² | 0.693 | 6.15 | 1500 mm  [stored 4.92126 ft] | 1190 mm  [stored 3.9042 ft] | 2090 mm  [stored 6.85696 ft] | 0.621 | 4.63 | No | 1190 mm  [stored 3.9042 ft] | 0.575 | 4.44 | 0.657 | 5.91 | 0 mm  [stored 0 ft] | 1500 mm  [stored 4.92126 ft] | 0.64 m² | 1133 mm | 717 mm | 717 mm | Yes | 2090 mm  [stored 6.85696 ft] | 1500 mm  [stored 4.92126 ft] |
| 1000SW-2112XOX-2000Pa | 0.64 m² | 0.64 m² | 0.693 | 6.15 | 2000 mm  [stored 6.56168 ft] | 1190 mm  [stored 3.9042 ft] | 2090 mm  [stored 6.85696 ft] | 0.621 | 4.63 | No | 1190 mm  [stored 3.9042 ft] | 0.575 | 4.44 | 0.657 | 5.91 | 0 mm  [stored 0 ft] | 1500 mm  [stored 4.92126 ft] | 0.64 m² | 1133 mm | 717 mm | 717 mm | Yes | 2090 mm  [stored 6.85696 ft] | 2000 mm  [stored 6.56168 ft] |
| 1000SW-2115XOX-1500Pa | 0.82 m² | 0.82 m² | 0.715 | 6.08 | 1500 mm  [stored 4.92126 ft] | 1490 mm  [stored 4.88845 ft] | 2090 mm  [stored 6.85696 ft] | 0.64 | 4.5 | Yes | 1490 mm  [stored 4.88845 ft] | 0.593 | 4.33 | 0.678 | 5.86 | 1 mm  [stored 0.00328084 ft] | 1500 mm  [stored 4.92126 ft] | 0.82 m² | 1433 mm | 717 mm | 717 mm | No | 2090 mm  [stored 6.85696 ft] | 1500 mm  [stored 4.92126 ft] |
| 1000SW-2115XOX-2000Pa | 0.82 m² | 0.82 m² | 0.715 | 6.08 | 2000 mm  [stored 6.56168 ft] | 1490 mm  [stored 4.88845 ft] | 2090 mm  [stored 6.85696 ft] | 0.64 | 4.5 | Yes | 1490 mm  [stored 4.88845 ft] | 0.593 | 4.33 | 0.678 | 5.86 | 1 mm  [stored 0.00328084 ft] | 1500 mm  [stored 4.92126 ft] | 0.82 m² | 1433 mm | 717 mm | 717 mm | No | 2090 mm  [stored 6.85696 ft] | 2000 mm  [stored 6.56168 ft] |
| 1000SW-2118XOX-1500Pa | 1.01 m² | 1.01 m² | 0.73 | 6.04 | 1500 mm  [stored 4.92126 ft] | 1790 mm  [stored 5.8727 ft] | 2090 mm  [stored 6.85696 ft] | 0.653 | 4.41 | Yes | 1790 mm  [stored 5.8727 ft] | 0.606 | 4.27 | 0.692 | 5.83 | 1 mm  [stored 0.00328084 ft] | 1500 mm  [stored 4.92126 ft] | 1.01 m² | 1733 mm | 717 mm | 717 mm | No | 2090 mm  [stored 6.85696 ft] | 1500 mm  [stored 4.92126 ft] |
| 1000SW-2118XOX-2000Pa | 1.01 m² | 1.01 m² | 0.73 | 6.04 | 2000 mm  [stored 6.56168 ft] | 1790 mm  [stored 5.8727 ft] | 2090 mm  [stored 6.85696 ft] | 0.653 | 4.41 | Yes | 1790 mm  [stored 5.8727 ft] | 0.606 | 4.27 | 0.692 | 5.83 | 1 mm  [stored 0.00328084 ft] | 1500 mm  [stored 4.92126 ft] | 1.01 m² | 1733 mm | 717 mm | 717 mm | No | 2090 mm  [stored 6.85696 ft] | 2000 mm  [stored 6.56168 ft] |
| 1000SW-2406XOX-1500Pa | 0.31 m² | 0.31 m² | 0.588 | 6.52 | 1500 mm  [stored 4.92126 ft] | 590 mm  [stored 1.9357 ft] | 2390 mm  [stored 7.84121 ft] | 0.528 | 5.26 | No | 590 mm  [stored 1.9357 ft] | 0.484 | 4.95 | 0.556 | 6.16 | 0 mm  [stored 0 ft] | 1500 mm  [stored 4.92126 ft] | 0.31 m² | 533 mm | 817 mm | 817 mm | Yes | 2390 mm  [stored 7.84121 ft] | 1500 mm  [stored 4.92126 ft] |
| 1000SW-2406XOX-2000Pa | 0.31 m² | 0.31 m² | 0.588 | 6.52 | 2000 mm  [stored 6.56168 ft] | 590 mm  [stored 1.9357 ft] | 2390 mm  [stored 7.84121 ft] | 0.528 | 5.26 | No | 590 mm  [stored 1.9357 ft] | 0.484 | 4.95 | 0.556 | 6.16 | 0 mm  [stored 0 ft] | 1500 mm  [stored 4.92126 ft] | 0.31 m² | 533 mm | 817 mm | 817 mm | Yes | 2390 mm  [stored 7.84121 ft] | 2000 mm  [stored 6.56168 ft] |
| 1000SW-2409XOX-1500Pa | 0.52 m² | 0.52 m² | 0.662 | 6.28 | 1500 mm  [stored 4.92126 ft] | 890 mm  [stored 2.91995 ft] | 2390 mm  [stored 7.84121 ft] | 0.593 | 4.82 | No | 890 mm  [stored 2.91995 ft] | 0.547 | 4.59 | 0.627 | 6 | 0 mm  [stored 0 ft] | 1500 mm  [stored 4.92126 ft] | 0.52 m² | 833 mm | 817 mm | 817 mm | Yes | 2390 mm  [stored 7.84121 ft] | 1500 mm  [stored 4.92126 ft] |
| 1000SW-2409XOX-2000Pa | 0.52 m² | 0.52 m² | 0.662 | 6.28 | 2000 mm  [stored 6.56168 ft] | 890 mm  [stored 2.91995 ft] | 2390 mm  [stored 7.84121 ft] | 0.593 | 4.82 | No | 890 mm  [stored 2.91995 ft] | 0.547 | 4.59 | 0.627 | 6 | 0 mm  [stored 0 ft] | 1500 mm  [stored 4.92126 ft] | 0.52 m² | 833 mm | 817 mm | 817 mm | Yes | 2390 mm  [stored 7.84121 ft] | 2000 mm  [stored 6.56168 ft] |
| 1000SW-2412XOX-1500Pa | 0.74 m² | 0.74 m² | 0.699 | 6.17 | 1500 mm  [stored 4.92126 ft] | 1190 mm  [stored 3.9042 ft] | 2390 mm  [stored 7.84121 ft] | 0.625 | 4.6 | No | 1190 mm  [stored 3.9042 ft] | 0.579 | 4.41 | 0.662 | 5.92 | 0 mm  [stored 0 ft] | 1500 mm  [stored 4.92126 ft] | 0.74 m² | 1133 mm | 817 mm | 817 mm | Yes | 2390 mm  [stored 7.84121 ft] | 1500 mm  [stored 4.92126 ft] |
| 1000SW-2412XOX-2000Pa | 0.74 m² | 0.74 m² | 0.699 | 6.17 | 2000 mm  [stored 6.56168 ft] | 1190 mm  [stored 3.9042 ft] | 2390 mm  [stored 7.84121 ft] | 0.625 | 4.6 | No | 1190 mm  [stored 3.9042 ft] | 0.579 | 4.41 | 0.662 | 5.92 | 0 mm  [stored 0 ft] | 1500 mm  [stored 4.92126 ft] | 0.74 m² | 1133 mm | 817 mm | 817 mm | Yes | 2390 mm  [stored 7.84121 ft] | 2000 mm  [stored 6.56168 ft] |
| 1000SW-2415XOX-1500Pa | 0.95 m² | 0.95 m² | 0.721 | 6.1 | 1500 mm  [stored 4.92126 ft] | 1490 mm  [stored 4.88845 ft] | 2390 mm  [stored 7.84121 ft] | 0.645 | 4.47 | Yes | 1490 mm  [stored 4.88845 ft] | 0.597 | 4.31 | 0.683 | 5.87 | 1 mm  [stored 0.00328084 ft] | 1500 mm  [stored 4.92126 ft] | 0.95 m² | 1433 mm | 817 mm | 817 mm | No | 2390 mm  [stored 7.84121 ft] | 1500 mm  [stored 4.92126 ft] |
| 1000SW-2415XOX-2000Pa | 0.95 m² | 0.95 m² | 0.721 | 6.1 | 2000 mm  [stored 6.56168 ft] | 1490 mm  [stored 4.88845 ft] | 2390 mm  [stored 7.84121 ft] | 0.645 | 4.47 | Yes | 1490 mm  [stored 4.88845 ft] | 0.597 | 4.31 | 0.683 | 5.87 | 1 mm  [stored 0.00328084 ft] | 1500 mm  [stored 4.92126 ft] | 0.95 m² | 1433 mm | 817 mm | 817 mm | No | 2390 mm  [stored 7.84121 ft] | 2000 mm  [stored 6.56168 ft] |
| 1000SW-2418XOX-1500Pa | 1.17 m² | 1.17 m² | 0.735 | 6.05 | 1500 mm  [stored 4.92126 ft] | 1790 mm  [stored 5.8727 ft] | 2390 mm  [stored 7.84121 ft] | 0.658 | 4.39 | Yes | 1790 mm  [stored 5.8727 ft] | 0.61 | 4.24 | 0.697 | 5.84 | 1 mm  [stored 0.00328084 ft] | 1500 mm  [stored 4.92126 ft] | 1.17 m² | 1733 mm | 817 mm | 817 mm | No | 2390 mm  [stored 7.84121 ft] | 1500 mm  [stored 4.92126 ft] |
| 1000SW-2418XOX-2000Pa | 1.17 m² | 1.17 m² | 0.735 | 6.05 | 2000 mm  [stored 6.56168 ft] | 1790 mm  [stored 5.8727 ft] | 2390 mm  [stored 7.84121 ft] | 0.658 | 4.39 | Yes | 1790 mm  [stored 5.8727 ft] | 0.61 | 4.24 | 0.697 | 5.84 | 1 mm  [stored 0.00328084 ft] | 1500 mm  [stored 4.92126 ft] | 1.17 m² | 1733 mm | 817 mm | 817 mm | No | 2390 mm  [stored 7.84121 ft] | 2000 mm  [stored 6.56168 ft] |
| 1000SW-2706XOX-1500Pa | 0.35 m² | 0.35 m² | 0.592 | 6.54 | 1500 mm  [stored 4.92126 ft] | 590 mm  [stored 1.9357 ft] | 2690 mm | 0.531 | 5.25 | No | 590 mm  [stored 1.9357 ft] | 0.487 | 4.94 | 0.559 | 6.17 | 0 mm  [stored 0 ft] | 1500 mm  [stored 4.92126 ft] | 0.35 m² | 533 mm | 917 mm | 917 mm | Yes | 2690 mm | 1500 mm  [stored 4.92126 ft] |
| 1000SW-2706XOX-2000Pa | 0.35 m² | 0.35 m² | 0.592 | 6.54 | 2000 mm  [stored 6.56168 ft] | 590 mm  [stored 1.9357 ft] | 2690 mm | 0.531 | 5.25 | No | 590 mm  [stored 1.9357 ft] | 0.487 | 4.94 | 0.559 | 6.17 | 0 mm  [stored 0 ft] | 1500 mm  [stored 4.92126 ft] | 0.35 m² | 533 mm | 917 mm | 917 mm | Yes | 2690 mm | 2000 mm  [stored 6.56168 ft] |
| 1000SW-2709XOX-1500Pa | 0.6 m² | 0.6 m² | 0.666 | 6.3 | 1500 mm  [stored 4.92126 ft] | 890 mm  [stored 2.91995 ft] | 2690 mm | 0.597 | 4.8 | No | 890 mm  [stored 2.91995 ft] | 0.55 | 4.57 | 0.631 | 6.01 | 0 mm  [stored 0 ft] | 1500 mm  [stored 4.92126 ft] | 0.6 m² | 833 mm | 917 mm | 917 mm | Yes | 2690 mm | 1500 mm  [stored 4.92126 ft] |
| 1000SW-2709XOX-2000Pa | 0.6 m² | 0.6 m² | 0.666 | 6.3 | 2000 mm  [stored 6.56168 ft] | 890 mm  [stored 2.91995 ft] | 2690 mm | 0.597 | 4.8 | No | 890 mm  [stored 2.91995 ft] | 0.55 | 4.57 | 0.631 | 6.01 | 0 mm  [stored 0 ft] | 1500 mm  [stored 4.92126 ft] | 0.6 m² | 833 mm | 917 mm | 917 mm | Yes | 2690 mm | 2000 mm  [stored 6.56168 ft] |
| 1000SW-2712XOX-1500Pa | 0.84 m² | 0.84 m² | 0.703 | 6.18 | 1500 mm  [stored 4.92126 ft] | 1190 mm  [stored 3.9042 ft] | 2690 mm | 0.629 | 4.58 | No | 1190 mm  [stored 3.9042 ft] | 0.582 | 4.39 | 0.666 | 5.93 | 0 mm  [stored 0 ft] | 1500 mm  [stored 4.92126 ft] | 0.84 m² | 1133 mm | 917 mm | 917 mm | Yes | 2690 mm | 1500 mm  [stored 4.92126 ft] |
| 1000SW-2712XOX-2000Pa | 0.84 m² | 0.84 m² | 0.703 | 6.18 | 2000 mm  [stored 6.56168 ft] | 1190 mm  [stored 3.9042 ft] | 2690 mm | 0.629 | 4.58 | No | 1190 mm  [stored 3.9042 ft] | 0.582 | 4.39 | 0.666 | 5.93 | 0 mm  [stored 0 ft] | 1500 mm  [stored 4.92126 ft] | 0.84 m² | 1133 mm | 917 mm | 917 mm | Yes | 2690 mm | 2000 mm  [stored 6.56168 ft] |
| 1000SW-2715XOX-1500Pa | 1.09 m² | 1.09 m² | 0.725 | 6.11 | 1500 mm  [stored 4.92126 ft] | 1490 mm  [stored 4.88845 ft] | 2690 mm | 0.648 | 4.45 | Yes | 1490 mm  [stored 4.88845 ft] | 0.601 | 4.29 | 0.687 | 5.88 | 1 mm  [stored 0.00328084 ft] | 1500 mm  [stored 4.92126 ft] | 1.09 m² | 1433 mm | 917 mm | 917 mm | No | 2690 mm | 1500 mm  [stored 4.92126 ft] |
| 1000SW-2715XOX-2000Pa | 1.09 m² | 1.09 m² | 0.725 | 6.11 | 2000 mm  [stored 6.56168 ft] | 1490 mm  [stored 4.88845 ft] | 2690 mm | 0.648 | 4.45 | Yes | 1490 mm  [stored 4.88845 ft] | 0.601 | 4.29 | 0.687 | 5.88 | 1 mm  [stored 0.00328084 ft] | 1500 mm  [stored 4.92126 ft] | 1.09 m² | 1433 mm | 917 mm | 917 mm | No | 2690 mm | 2000 mm  [stored 6.56168 ft] |
| 1000SW-2718XOX-1500Pa | 1.33 m² | 1.33 m² | 0.74 | 6.06 | 1500 mm  [stored 4.92126 ft] | 1790 mm  [stored 5.8727 ft] | 2690 mm | 0.661 | 4.36 | Yes | 1790 mm  [stored 5.8727 ft] | 0.613 | 4.21 | 0.701 | 5.85 | 1 mm  [stored 0.00328084 ft] | 1500 mm  [stored 4.92126 ft] | 1.33 m² | 1733 mm | 917 mm | 917 mm | No | 2690 mm | 1500 mm  [stored 4.92126 ft] |
| 1000SW-2718XOX-2000Pa | 1.33 m² | 1.33 m² | 0.74 | 6.06 | 2000 mm  [stored 6.56168 ft] | 1790 mm  [stored 5.8727 ft] | 2690 mm | 0.661 | 4.36 | Yes | 1790 mm  [stored 5.8727 ft] | 0.613 | 4.21 | 0.701 | 5.85 | 1 mm  [stored 0.00328084 ft] | 1500 mm  [stored 4.92126 ft] | 1.33 m² | 1733 mm | 917 mm | 917 mm | No | 2690 mm | 2000 mm  [stored 6.56168 ft] |
| 1000SW-3006XOX-1500Pa | 0.4 m² | 0.4 m² | 0.595 | 6.55 | 1500 mm  [stored 4.92126 ft] | 590 mm  [stored 1.9357 ft] | 2990 mm  [stored 9.80971 ft] | 0.533 | 5.24 | No | 590 mm  [stored 1.9357 ft] | 0.489 | 4.93 | 0.562 | 6.18 | 0 mm  [stored 0 ft] | 1500 mm  [stored 4.92126 ft] | 0.4 m² | 533 mm | 1017 mm | 1017 mm | Yes | 2990 mm  [stored 9.80971 ft] | 1500 mm  [stored 4.92126 ft] |
| 1000SW-3006XOX-2000Pa | 0.4 m² | 0.4 m² | 0.595 | 6.55 | 2000 mm  [stored 6.56168 ft] | 590 mm  [stored 1.9357 ft] | 2990 mm  [stored 9.80971 ft] | 0.533 | 5.24 | No | 590 mm  [stored 1.9357 ft] | 0.489 | 4.93 | 0.562 | 6.18 | 0 mm  [stored 0 ft] | 1500 mm  [stored 4.92126 ft] | 0.4 m² | 533 mm | 1017 mm | 1017 mm | Yes | 2990 mm  [stored 9.80971 ft] | 2000 mm  [stored 6.56168 ft] |
| 1000SW-3009XOX-1500Pa | 0.67 m² | 0.67 m² | 0.669 | 6.31 | 1500 mm  [stored 4.92126 ft] | 890 mm  [stored 2.91995 ft] | 2990 mm  [stored 9.80971 ft] | 0.599 | 4.79 | No | 890 mm  [stored 2.91995 ft] | 0.553 | 4.56 | 0.634 | 6.02 | 0 mm  [stored 0 ft] | 1500 mm  [stored 4.92126 ft] | 0.67 m² | 833 mm | 1017 mm | 1017 mm | Yes | 2990 mm  [stored 9.80971 ft] | 1500 mm  [stored 4.92126 ft] |
| 1000SW-3009XOX-2000Pa | 0.67 m² | 0.67 m² | 0.669 | 6.31 | 2000 mm  [stored 6.56168 ft] | 890 mm  [stored 2.91995 ft] | 2990 mm  [stored 9.80971 ft] | 0.599 | 4.79 | No | 890 mm  [stored 2.91995 ft] | 0.553 | 4.56 | 0.634 | 6.02 | 0 mm  [stored 0 ft] | 1500 mm  [stored 4.92126 ft] | 0.67 m² | 833 mm | 1017 mm | 1017 mm | Yes | 2990 mm  [stored 9.80971 ft] | 2000 mm  [stored 6.56168 ft] |
| 1000SW-3012XOX-1500Pa | 0.95 m² | 0.95 m² | 0.706 | 6.19 | 1500 mm  [stored 4.92126 ft] | 1190 mm  [stored 3.9042 ft] | 2990 mm  [stored 9.80971 ft] | 0.632 | 4.57 | No | 1190 mm  [stored 3.9042 ft] | 0.584 | 4.38 | 0.669 | 5.94 | 0 mm  [stored 0 ft] | 1500 mm  [stored 4.92126 ft] | 0.95 m² | 1133 mm | 1017 mm | 1017 mm | Yes | 2990 mm  [stored 9.80971 ft] | 1500 mm  [stored 4.92126 ft] |
| 1000SW-3012XOX-2000Pa | 0.95 m² | 0.95 m² | 0.706 | 6.19 | 2000 mm  [stored 6.56168 ft] | 1190 mm  [stored 3.9042 ft] | 2990 mm  [stored 9.80971 ft] | 0.632 | 4.57 | No | 1190 mm  [stored 3.9042 ft] | 0.584 | 4.38 | 0.669 | 5.94 | 0 mm  [stored 0 ft] | 1500 mm  [stored 4.92126 ft] | 0.95 m² | 1133 mm | 1017 mm | 1017 mm | Yes | 2990 mm  [stored 9.80971 ft] | 2000 mm  [stored 6.56168 ft] |
| 1000SW-3015XOX-1500Pa | 1.22 m² | 1.22 m² | 0.728 | 6.11 | 1500 mm  [stored 4.92126 ft] | 1490 mm  [stored 4.88845 ft] | 2990 mm  [stored 9.80971 ft] | 0.651 | 4.44 | Yes | 1490 mm  [stored 4.88845 ft] | 0.603 | 4.207 | 0.69 | 5.89 | 1 mm  [stored 0.00328084 ft] | 1500 mm  [stored 4.92126 ft] | 1.22 m² | 1433 mm | 1017 mm | 1017 mm | No | 2990 mm  [stored 9.80971 ft] | 1500 mm  [stored 4.92126 ft] |
| 1000SW-3015XOX-2000Pa | 1.22 m² | 1.22 m² | 0.728 | 6.11 | 2000 mm  [stored 6.56168 ft] | 1490 mm  [stored 4.88845 ft] | 2990 mm  [stored 9.80971 ft] | 0.651 | 4.44 | Yes | 1490 mm  [stored 4.88845 ft] | 0.603 | 4.207 | 0.69 | 5.89 | 1 mm  [stored 0.00328084 ft] | 1500 mm  [stored 4.92126 ft] | 1.22 m² | 1433 mm | 1017 mm | 1017 mm | No | 2990 mm  [stored 9.80971 ft] | 2000 mm  [stored 6.56168 ft] |
| 1000SW-3018XOX-1500Pa | 1.49 m² | 1.5 m² | 0.743 | 6.07 | 1500 mm  [stored 4.92126 ft] | 1790 mm  [stored 5.8727 ft] | 2990 mm  [stored 9.80971 ft] | 0.664 | 4.35 | Yes | 1790 mm  [stored 5.8727 ft] | 0.616 | 4.2 | 0.704 | 5.86 | 1 mm  [stored 0.00328084 ft] | 1500 mm  [stored 4.92126 ft] | 1.5 m² | 1733 mm | 1017 mm | 1017 mm | No | 2990 mm  [stored 9.80971 ft] | 1500 mm  [stored 4.92126 ft] |
| 1000SW-3018XOX-2000Pa | 1.49 m² | 1.5 m² | 0.743 | 6.07 | 2000 mm  [stored 6.56168 ft] | 1790 mm  [stored 5.8727 ft] | 2990 mm  [stored 9.80971 ft] | 0.664 | 4.35 | Yes | 1790 mm  [stored 5.8727 ft] | 0.616 | 4.2 | 0.704 | 5.86 | 1 mm  [stored 0.00328084 ft] | 1500 mm  [stored 4.92126 ft] | 1.5 m² | 1733 mm | 1017 mm | 1017 mm | No | 2990 mm  [stored 9.80971 ft] | 2000 mm  [stored 6.56168 ft] |

note: [stored X ft] marks values corroborated as IEEE doubles in the binary element streams (Revit-internal decimal feet)

## geometry (parser evidence)
native form markers: Sweep x10
no freeform markers — native parametric forms only
